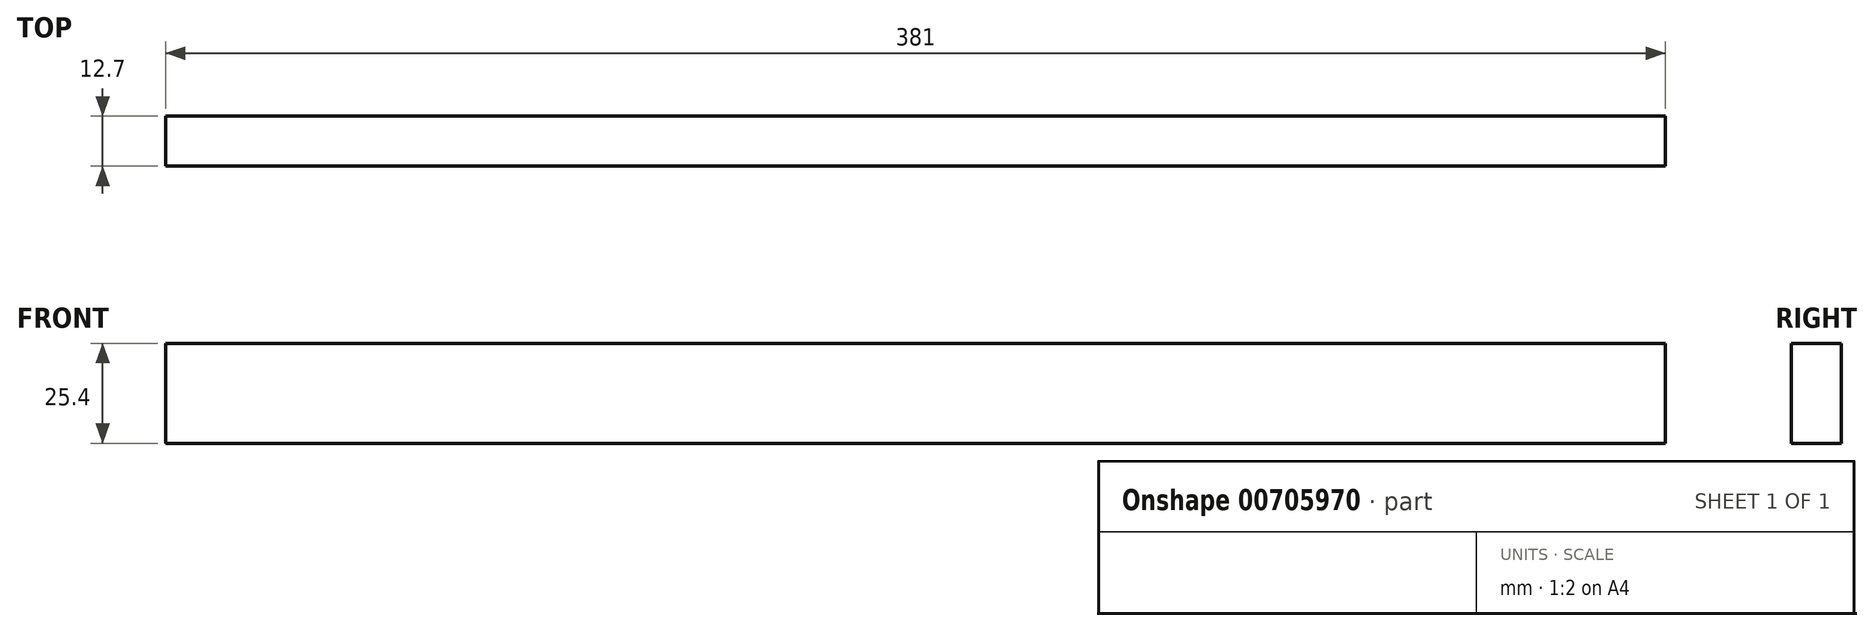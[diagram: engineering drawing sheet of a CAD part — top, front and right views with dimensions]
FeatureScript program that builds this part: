
annotation { "Feature Type Name" : "Feature", "Feature Type Description" : "" }
export const myFeature = defineFeature(function(context is Context, id is Id, definition is map)
    precondition{}
    {
        {
            var Q0;
            Q0=qCreatedBy(makeId("Top.planeOp"),FACE);
            var sketch = newSketch(context, id + "F0", { "sketchPlane" : qUnion([Q0])});
            skLineSegment(sketch, "E0.bottom", {"start": v(-71, 39.99) * mm, "end": v(310, 39.99) * mm});
            skLineSegment(sketch, "E0.top", {"start": v(-71, 27.29) * mm, "end": v(310, 27.29) * mm});
            skLineSegment(sketch, "E0.left", {"start": v(-71, 39.99) * mm, "end": v(-71, 27.29) * mm});
            skLineSegment(sketch, "E0.right", {"start": v(310, 39.99) * mm, "end": v(310, 27.29) * mm});
            skSolve(sketch);
        }
        {
            var Q0;
            Q0 = qSketchRegion(id + "F0", true);
            extrude(context, id + "F1", {"entities" : qUnion([Q0]), "depth" : 25.4 * mm, "offsetDistance" : 25.4 * mm});
        }
    });
